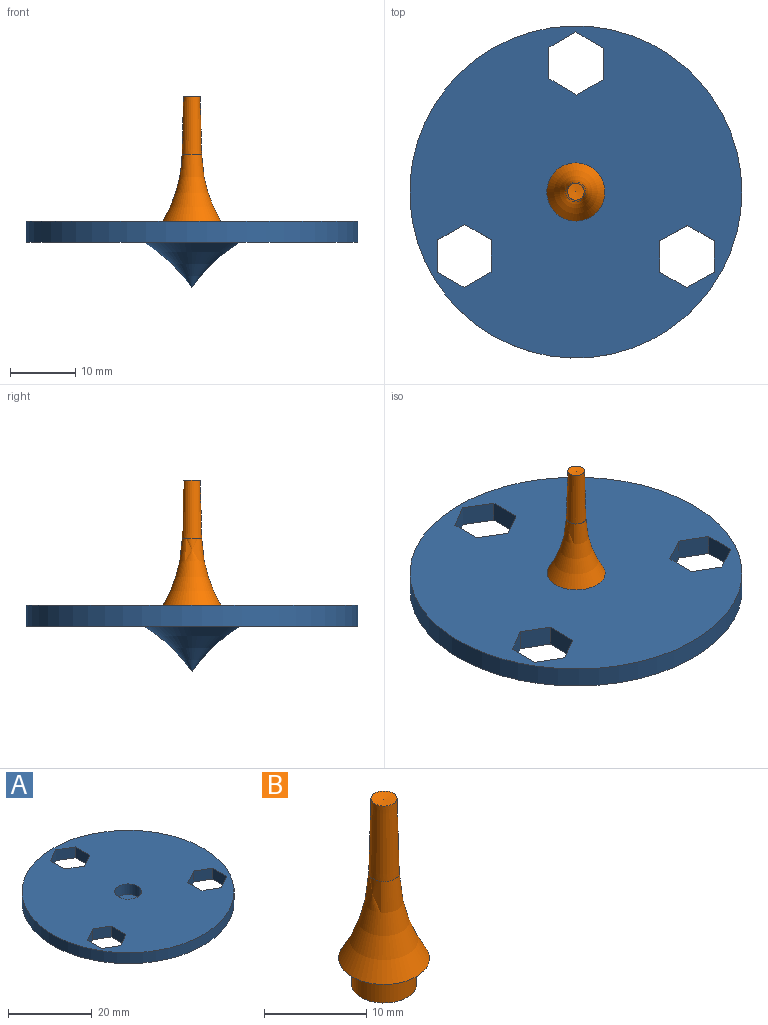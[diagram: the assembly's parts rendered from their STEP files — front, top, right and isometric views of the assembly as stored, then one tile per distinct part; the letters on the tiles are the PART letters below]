
ASSEMBLY  parts=2 mates=1
PART A: 24 faces, bbox 50.8x50.8x10.3 mm
  f0: plane 50.8x50.8mm, normal (0,0,1), area 1815.3mm2, adj f3,f4,f5,f6,f7,f8,f9,f10
  f1: plane 50.8x50.8mm, normal (0,0,-1), area 1676.4mm2, adj f2,f3,f4,f5,f6,f7,f8,f9
  f2: torus R=19.24mm, axis (0,0,1), area 220.4mm2, adj f1
  f3: cylinder r=25.4mm len=50.8mm, axis (0,0,1), area 506.7mm2, adj f0,f1
  f4: plane 4.75x3.18mm, normal (1,0,0), area 15.1mm2, adj f0,f1,f5,f9
  f5: plane 4.12x3.18mm, normal (0.5,0.87,0), area 15.1mm2, adj f0,f1,f4,f6
  f6: plane 4.29x3.18mm, normal (-0.48,0.87,0), area 15.6mm2, adj f0,f1,f5,f7
  f7: plane 4.75x3.18mm, normal (-1,0,0), area 15.1mm2, adj f0,f1,f6,f8
  f8: plane 4.12x3.18mm, normal (-0.5,-0.87,0), area 15.1mm2, adj f0,f1,f7,f9
  f9: plane 4.29x3.18mm, normal (0.48,-0.87,0), area 15.6mm2, adj f0,f1,f4,f8
  f10: plane 4.12x3.18mm, normal (-0.5,-0.87,0), area 15.1mm2, adj f0,f1,f11,f15
  f11: plane 4.12x3.18mm, normal (0.5,-0.87,0), area 15.1mm2, adj f0,f1,f10,f12
  f12: plane 4.9x3.18mm, normal (1,-0.02,0), area 15.6mm2, adj f0,f1,f11,f13
  f13: plane 4.12x3.18mm, normal (0.5,0.87,0), area 15.1mm2, adj f0,f1,f12,f14
  f14: plane 4.12x3.18mm, normal (-0.5,0.87,0), area 15.1mm2, adj f0,f1,f13,f15
  f15: plane 4.9x3.18mm, normal (-1,0.02,0), area 15.6mm2, adj f0,f1,f10,f14
  f16: plane 4.2x3.18mm, normal (0.52,0.86,0), area 15.6mm2, adj f0,f1,f17,f21
  f17: plane 4.12x3.18mm, normal (-0.5,0.87,0), area 15.1mm2, adj f0,f1,f16,f18
  f18: plane 4.75x3.18mm, normal (-1,0,0), area 15.1mm2, adj f0,f1,f17,f19
  f19: plane 4.2x3.18mm, normal (-0.52,-0.86,0), area 15.6mm2, adj f0,f1,f18,f20
  f20: plane 4.12x3.18mm, normal (0.5,-0.87,0), area 15.1mm2, adj f0,f1,f19,f21
  f21: plane 4.75x3.18mm, normal (1,0,0), area 15.1mm2, adj f0,f1,f16,f20
  f22: cylinder r=3.17mm len=6.35mm, axis (0,0,1), area 62.3mm2, adj f0,f23
  f23: plane 6.35x6.35mm, normal (0,0,1), area 31.7mm2, adj f22
PART B: 6 faces, bbox 16.4x16.4x23.3 mm
  f0: plane 6.35x6.35mm, normal (0,0,-1), area 31.7mm2, adj f1
  f1: cylinder r=3.17mm len=6.35mm, axis (0,0,-1), area 62.3mm2, adj f0,f2
  f2: plane 8.89x8.89mm, normal (0,0,-1), area 30.4mm2, adj f1,f3
  f3: torus R=22.54mm, axis (0,0,-1), area 171.4mm2, adj f2,f4
  f4: cone r=1.49mm half-angle=1.4deg, axis (0,0,-1), area 77.5mm2, adj f3,f5
  f5: cone r=1.28mm half-angle=85.2deg, axis (0,0,1), area 5.1mm2, adj f4
PLACE A t=(-6.67,0.85,-4.09)mm
PLACE B t=(-6.67,0.85,6.92)mm
MATE fastened B.f1 <-> A.f22  axis (0,0,-1) through (-6.67,0.85,6.92)mm
